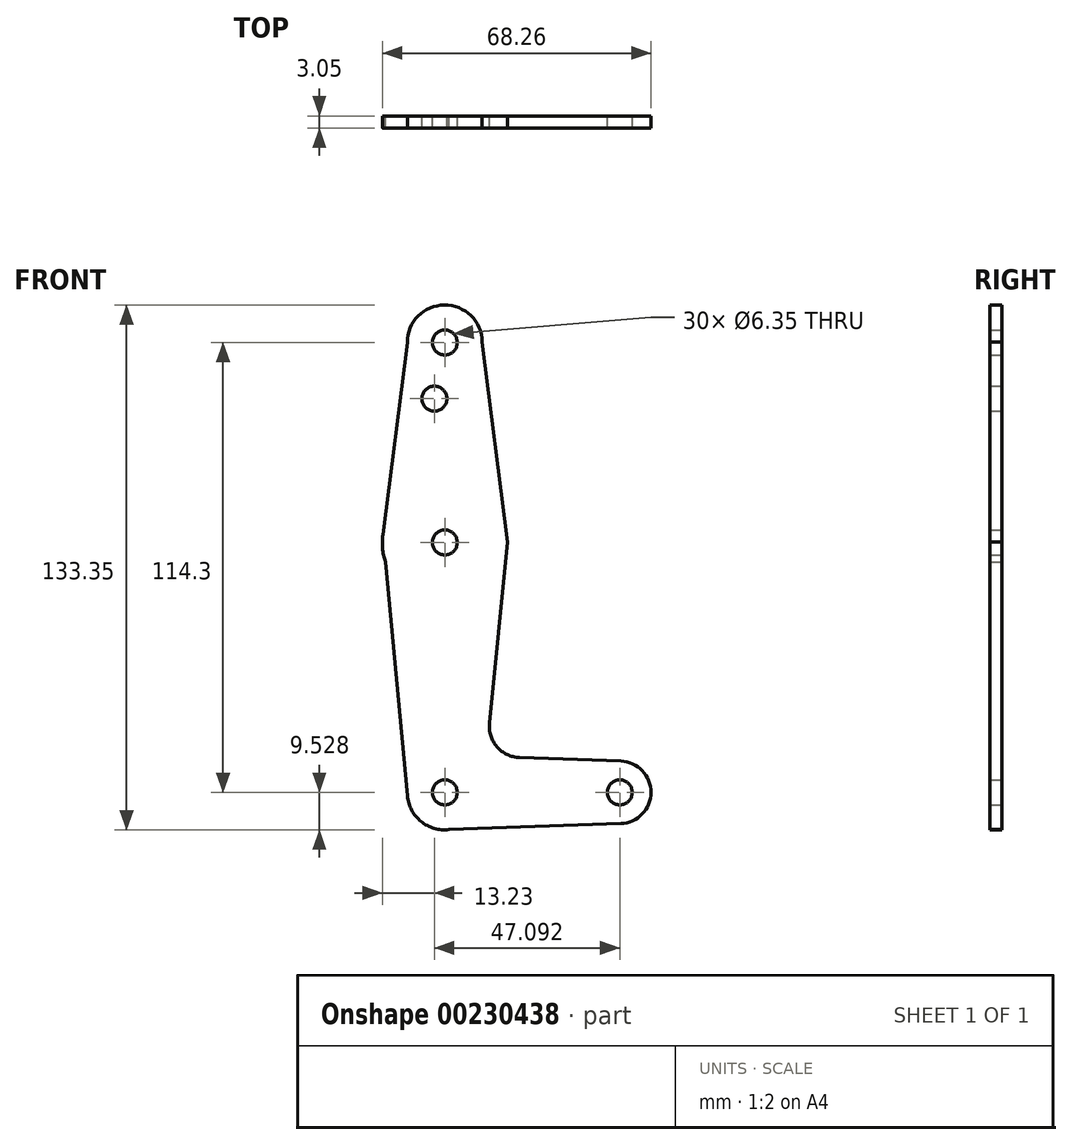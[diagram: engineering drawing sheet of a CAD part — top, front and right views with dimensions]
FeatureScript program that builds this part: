
annotation { "Feature Type Name" : "Feature", "Feature Type Description" : "" }
export const myFeature = defineFeature(function(context is Context, id is Id, definition is map)
    precondition{}
    {
        {
            var Q0;
            Q0=qCreatedBy(makeId("Front.planeOp"),FACE);
            var sketch = newSketch(context, id + "F0", { "sketchPlane" : qUnion([Q0])});
            skLineSegment(sketch, "E0", {"start": v(-47.64, 70.67) * mm, "end": v(-47.64, -43.63) * mm, "construction": true});
            skLineSegment(sketch, "E1", {"start": v(-47.64, -43.63) * mm, "end": v(-3.19, -43.63) * mm, "construction": true});
            skCircle(sketch, "E2", {"center": v(-47.64, 70.67) * mm, "radius": 9.53 * mm});
            skCircle(sketch, "E3", {"center": v(-47.64, 19.87) * mm, "radius": 15.88 * mm});
            skCircle(sketch, "E4", {"center": v(-47.64, -43.63) * mm, "radius": 9.53 * mm});
            skCircle(sketch, "E5", {"center": v(-3.19, -43.63) * mm, "radius": 7.94 * mm});
            skLineSegment(sketch, "E6", {"start": v(-57.16, 70.67) * mm, "end": v(-63.39, 21.88) * mm});
            skLineSegment(sketch, "E7", {"start": v(-63.39, 21.88) * mm, "end": v(-57.12, -44.53) * mm});
            skLineSegment(sketch, "E8", {"start": v(-48.04, -53.15) * mm, "end": v(-2.9, -51.56) * mm});
            skLineSegment(sketch, "E9", {"start": v(-28.66, -34.78) * mm, "end": v(-2.9, -35.7) * mm});
            skLineSegment(sketch, "E10", {"start": v(-38.11, 70.84) * mm, "end": v(-31.65, 19.95) * mm});
            skLineSegment(sketch, "E11", {"start": v(-31.65, 19.95) * mm, "end": v(-36.29, -26.04) * mm});
            skCircle(sketch, "E12", {"center": v(-47.64, 70.67) * mm, "radius": 3.18 * mm});
            skCircle(sketch, "E13", {"center": v(-47.64, 19.87) * mm, "radius": 3.18 * mm});
            skCircle(sketch, "E14", {"center": v(-47.64, -43.63) * mm, "radius": 3.18 * mm});
            skCircle(sketch, "E15", {"center": v(-3.19, -43.63) * mm, "radius": 3.18 * mm});
            skArc(sketch, "E16.filletArc", {"start": v(-36.29, -26.04) * mm, "mid": v(-34.37, -32.06) * mm, "end": v(-28.66, -34.78) * mm});
            skCircle(sketch, "E17", {"center": v(-50.28, 56.4) * mm, "radius": 3.18 * mm});
            skSolve(sketch);
        }
        {
            var Q0;
            Q0 = qSketchRegion(id + "F0", true);
            extrude(context, id + "F1", {"entities" : qUnion([Q0]), "depth" : 3.05 * mm, "hasSecondDirectionDraft" : true, "secondDirectionDraftAngle" : 3 * degree});
        }
    });
